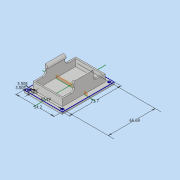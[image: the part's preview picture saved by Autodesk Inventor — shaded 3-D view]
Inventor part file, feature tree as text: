
AUTODESK INVENTOR PART (.ipt)
format: ipt  version: 2017 (Build 210142000, 142)  size: 140,288 bytes
history: native  units: in
note: dims shown in document units (in); Inventor stores cm internally (conversion verified against a paired STEP export)
features: extrude x4, sketch x3, plane x1, fillet x1
ambient origin geometry x8: Origin, YZ Plane, XZ Plane, XY Plane, X Axis, Y Axis, Z Axis, Center Point
bodies: Solid1 (feature_tree)
feature tree (9):
  sketch  "Sketch1"  dims[d0=2.1339in d1=2.9016in]
  extrude  "baseplate"  Depth=2.9016in
  extrude  "perimeter"  Depth=1.4961in
  plane  "Work Plane1"
  extrude  "holders"  Depth=0.0787in
  extrude  "Extrusion4"  Depth=0.3937in TaperAngle=0.0deg
  fillet  "Fillet1"  Radius=0.0787in
  sketch  "Sketch2"  dims[d2=0.125in d3=0.0in d4=1.4961in]
  sketch  "Sketch3"  dims[d5=2.2244in d6=0.0787in d7=0.3937in d8=0.0in d10=0.0787in d11=0.0787in d12=0.3543in d13=0.5118in d14=1.0236in d15=0.0in d16=0.138in d17=0.138in d18=0.138in d19=0.7874in d21=1.8579in d22=0.7874in d24=2.6256in d27=0.3937in d28=0.0in d29=0.1969in]
